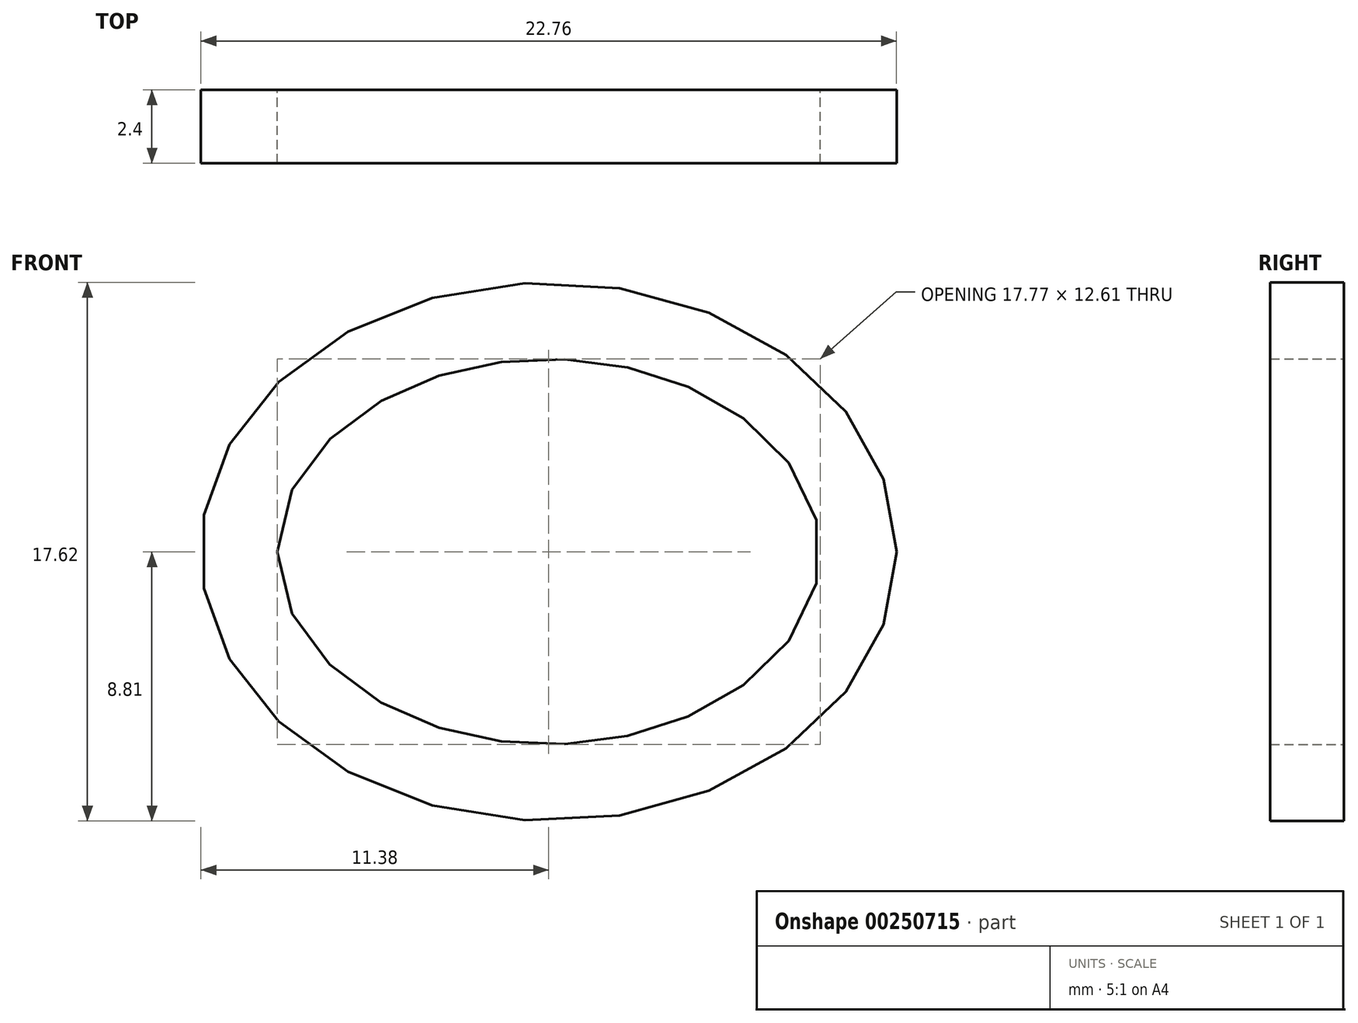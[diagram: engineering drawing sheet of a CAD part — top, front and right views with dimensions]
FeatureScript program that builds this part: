
annotation { "Feature Type Name" : "Feature", "Feature Type Description" : "" }
export const myFeature = defineFeature(function(context is Context, id is Id, definition is map)
    precondition{}
    {
        {
            var Q0;
            Q0=qCreatedBy(makeId("Front.planeOp"),FACE);
            var sketch = newSketch(context, id + "F0", { "sketchPlane" : qUnion([Q0])});
            skEllipse(sketch, "E0", {"center": v(0, 0) * mm, "majorRadius": 11.38 * mm, "minorRadius": 8.8 * mm, "majorAxis": v(1, 0)});
            skSolve(sketch);
        }
        {
            var Q0;
            Q0=makeQuery(id+"F0.imprint","IMPRINT",FACE,{"disambiguationData":[TD([[makeQuery(id+"F0.imprint","IMPRINT",EDGE,{"derivedFrom":sQuery(id+"F0.wireOp",EDGE,"E0")}),1.0]])]});
            extrude(context, id + "F1", {"entities" : qUnion([Q0]), "depth" : 2.4 * mm});
        }
        {
            var Q0;
            Q0=makeQuery(id+"F1.opExtrude","CAP_FACE",FACE,{"disambiguationData":[OSD([sQuery(id+"F0.wireOp",EDGE,"E0")])],"isStart":false});
            var Q1;
            Q1=makeQuery(id+"F1.opExtrude","CAP_FACE",FACE,{"disambiguationData":[OSD([sQuery(id+"F0.wireOp",EDGE,"E0")])],"isStart":true});
            shell(context, id + "F2", {"entities" : qUnion([Q0, Q1]), "thickness" : 2.5 * mm});
        }
    });
